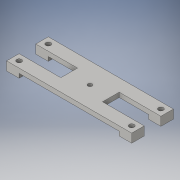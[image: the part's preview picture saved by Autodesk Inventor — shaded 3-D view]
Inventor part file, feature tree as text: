
AUTODESK INVENTOR PART (.ipt)
format: ipt  version: 2016 (Build 200138000, 138)  size: 170,496 bytes
history: native  units: in
note: dims shown in document units (in); Inventor stores cm internally (conversion verified against a paired STEP export)
features: extrude x5, sketch x5
ambient origin geometry x8: Origin, YZ Plane, XZ Plane, XY Plane, X Axis, Y Axis, Z Axis, Center Point
bodies: Solid1 (feature_tree)
feature tree (10):
  extrude  "Extrusion1"  Depth=1.0in
  extrude  "Extrusion2"  Depth=0.3in
  extrude  "Extrusion3"  Depth=1.0in TaperAngle=0.0deg
  extrude  "Extrusion4"  Depth=1.0in TaperAngle=0.0deg
  extrude  "Extrusion5"  Depth=0.3in
  sketch  "Sketch1"  dims[d0=1.0in d1=1.0in]
  sketch  "Sketch2"  dims[d2=0.11in d3=0.0in d4=0.3in]
  sketch  "Sketch3"  dims[d5=0.3in d6=1.0in d7=2.0in d8=0.0in d9=0.0in]
  sketch  "Sketch4"  dims[d10=0.1in d11=1.0in d12=0.0in]
  sketch  "Sketch5"  dims[d13=0.3in d14=0.3in d15=0.3in d16=0.1in d17=0.0in d18=0.1181in d19=0.1181in d20=0.1182in d21=0.1181in d22=3.0in d23=0.0in]
